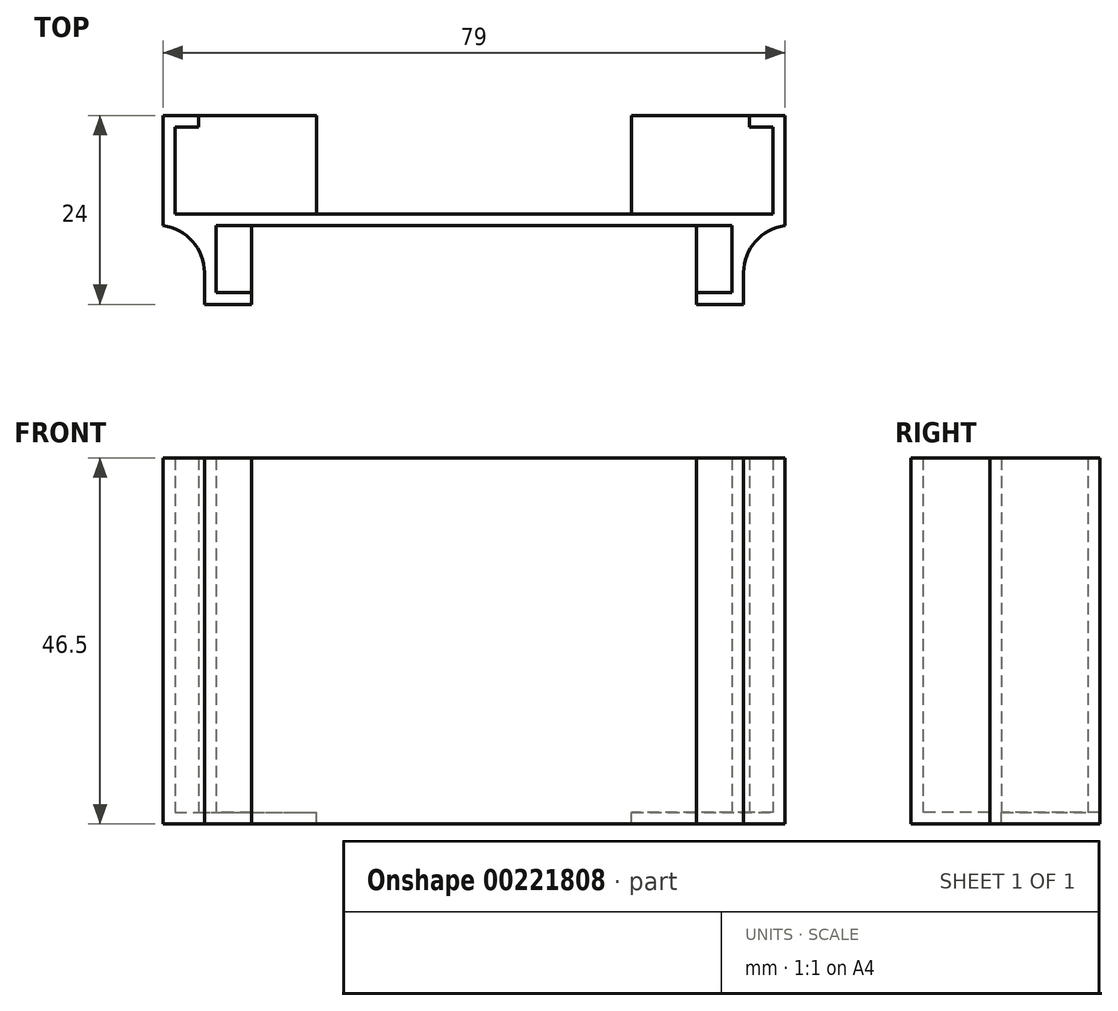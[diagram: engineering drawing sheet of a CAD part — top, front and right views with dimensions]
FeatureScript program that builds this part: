
annotation { "Feature Type Name" : "Feature", "Feature Type Description" : "" }
export const myFeature = defineFeature(function(context is Context, id is Id, definition is map)
    precondition{}
    {
        {
            var Q0;
            Q0=qCreatedBy(makeId("Top.planeOp"),FACE);
            var sketch = newSketch(context, id + "F0", { "sketchPlane" : qUnion([Q0])});
            skLineSegment(sketch, "E0", {"start": v(0, 0) * mm, "end": v(-38, 0) * mm});
            skLineSegment(sketch, "E1", {"start": v(-38, 0) * mm, "end": v(-38, 11) * mm});
            skLineSegment(sketch, "E2", {"start": v(-38, 11) * mm, "end": v(-35, 11) * mm});
            skLineSegment(sketch, "E3.0", {"start": v(-39.5, 12.5) * mm, "end": v(-35, 12.5) * mm});
            skLineSegment(sketch, "E3.1", {"start": v(-39.5, -1.5) * mm, "end": v(-39.5, 12.5) * mm});
            skLineSegment(sketch, "E3.2", {"start": v(0, -1.5) * mm, "end": v(-39.5, -1.5) * mm});
            skLineSegment(sketch, "E4", {"start": v(-35, 12.5) * mm, "end": v(-35, 11) * mm});
            skLineSegment(sketch, "E5.MirrorCS", {"start": v(0, 0) * mm, "end": v(38, 0) * mm});
            skLineSegment(sketch, "E6.MirrorCS", {"start": v(38, 0) * mm, "end": v(38, 11) * mm});
            skLineSegment(sketch, "E7.MirrorCS", {"start": v(38, 11) * mm, "end": v(35, 11) * mm});
            skLineSegment(sketch, "E8.MirrorCS", {"start": v(35, 12.5) * mm, "end": v(35, 11) * mm});
            skLineSegment(sketch, "E9.MirrorCS", {"start": v(39.5, 12.5) * mm, "end": v(35, 12.5) * mm});
            skLineSegment(sketch, "E10.MirrorCS", {"start": v(39.5, -1.5) * mm, "end": v(39.5, 12.5) * mm});
            skLineSegment(sketch, "E11.MirrorCS", {"start": v(0, -1.5) * mm, "end": v(39.5, -1.5) * mm});
            skLineSegment(sketch, "E12", {"start": v(-32.75, -1.5) * mm, "end": v(-32.75, -10) * mm});
            skLineSegment(sketch, "E13", {"start": v(-32.75, -10) * mm, "end": v(-28.25, -10) * mm});
            skLineSegment(sketch, "E14.0", {"start": v(-34.25, -11.5) * mm, "end": v(-28.25, -11.5) * mm});
            skLineSegment(sketch, "E14.1", {"start": v(-34.25, -1.5) * mm, "end": v(-34.25, -11.5) * mm});
            skLineSegment(sketch, "E15", {"start": v(-28.25, -10) * mm, "end": v(-28.25, -11.5) * mm});
            skLineSegment(sketch, "E16.MirrorCS", {"start": v(34.25, -1.5) * mm, "end": v(34.25, -11.5) * mm});
            skLineSegment(sketch, "E17.MirrorCS", {"start": v(32.75, -1.5) * mm, "end": v(32.75, -10) * mm});
            skLineSegment(sketch, "E18.MirrorCS", {"start": v(32.75, -10) * mm, "end": v(28.25, -10) * mm});
            skLineSegment(sketch, "E19.MirrorCS", {"start": v(34.25, -11.5) * mm, "end": v(28.25, -11.5) * mm});
            skLineSegment(sketch, "E20.MirrorCS", {"start": v(28.25, -10) * mm, "end": v(28.25, -11.5) * mm});
            skSolve(sketch);
        }
        {
            var Q0;
            Q0=makeQuery(id+"F0.imprint","IMPRINT",FACE,{"disambiguationData":[TD([[makeQuery(id+"F0.imprint","IMPRINT",EDGE,{"derivedFrom":sQuery(id+"F0.wireOp",EDGE,"E0")}),1.0]])]});
            var Q1;
            {var subQ0=sQuery(id+"F0.wireOp",EDGE,"E12");Q1=makeQuery(id+"F0.imprint","IMPRINT",FACE,{"disambiguationData":[TD([[makeQuery(id+"F0.imprint","IMPRINT",EDGE,{"derivedFrom":subQ0}),-1.0]])]});}
            var Q2;
            {var subQ1=sQuery(id+"F0.wireOp",EDGE,"E16.MirrorCS");Q2=makeQuery(id+"F0.imprint","IMPRINT",FACE,{"disambiguationData":[TD([[makeQuery(id+"F0.imprint","IMPRINT",EDGE,{"derivedFrom":subQ1}),-1.0]])]});}
            extrude(context, id + "F1", {"entities" : qUnion([Q0, Q1, Q2]), "depth" : 45 * mm});
        }
        {
            var Q0;
            Q0=makeQuery(id+"F1.opExtrude","SWEPT_EDGE",EDGE,{"disambiguationData":[OSD([sQuery(id+"F0.wireOp",EDGE,"E3.2"),sQuery(id+"F0.wireOp",EDGE,"E14.1")])]});
            var Q1;
            Q1=makeQuery(id+"F1.opExtrude","SWEPT_EDGE",EDGE,{"disambiguationData":[OSD([sQuery(id+"F0.wireOp",EDGE,"E11.MirrorCS"),sQuery(id+"F0.wireOp",EDGE,"E16.MirrorCS")])]});
            fillet(context, id + "F2", {"entities" : qUnion([Q0, Q1]), "radius" : 6 * mm, "tangentPropagation" : true, "allowEdgeOverflow" : false});
        }
        {
            var Q0;
            Q0=makeQuery(id+"F1.opExtrude","CAP_FACE",FACE,{"disambiguationData":[OSD([sQuery(id+"F0.wireOp",EDGE,"E0"),sQuery(id+"F0.wireOp",EDGE,"E1"),sQuery(id+"F0.wireOp",EDGE,"E2"),sQuery(id+"F0.wireOp",EDGE,"E3.0"),sQuery(id+"F0.wireOp",EDGE,"E3.1"),sQuery(id+"F0.wireOp",EDGE,"E3.2"),sQuery(id+"F0.wireOp",EDGE,"E4"),sQuery(id+"F0.wireOp",EDGE,"E5.MirrorCS"),sQuery(id+"F0.wireOp",EDGE,"E6.MirrorCS"),sQuery(id+"F0.wireOp",EDGE,"E7.MirrorCS"),sQuery(id+"F0.wireOp",EDGE,"E8.MirrorCS"),sQuery(id+"F0.wireOp",EDGE,"E9.MirrorCS"),sQuery(id+"F0.wireOp",EDGE,"E10.MirrorCS"),sQuery(id+"F0.wireOp",EDGE,"E11.MirrorCS"),sQuery(id+"F0.wireOp",EDGE,"E12"),sQuery(id+"F0.wireOp",EDGE,"E13"),sQuery(id+"F0.wireOp",EDGE,"E14.0"),sQuery(id+"F0.wireOp",EDGE,"E14.1"),sQuery(id+"F0.wireOp",EDGE,"E15"),sQuery(id+"F0.wireOp",EDGE,"E16.MirrorCS"),sQuery(id+"F0.wireOp",EDGE,"E17.MirrorCS"),sQuery(id+"F0.wireOp",EDGE,"E18.MirrorCS"),sQuery(id+"F0.wireOp",EDGE,"E19.MirrorCS"),sQuery(id+"F0.wireOp",EDGE,"E20.MirrorCS")])],"isStart":true});
            var sketch = newSketch(context, id + "F3", { "sketchPlane" : qUnion([Q0])});
            skLineSegment(sketch, "E21", {"start": v(-35, -12.5) * mm, "end": v(-20, -12.5) * mm});
            skLineSegment(sketch, "E22", {"start": v(-20, -12.5) * mm, "end": v(-20, 0) * mm});
            skLineSegment(sketch, "E23", {"start": v(-28.25, 10) * mm, "end": v(-28.25, 1.5) * mm});
            skLineSegment(sketch, "E24.MirrorCS", {"start": v(28.25, 10) * mm, "end": v(28.25, 1.5) * mm});
            skLineSegment(sketch, "E25.MirrorCS", {"start": v(20, -12.5) * mm, "end": v(20, 0) * mm});
            skLineSegment(sketch, "E26.MirrorCS", {"start": v(35, -12.5) * mm, "end": v(20, -12.5) * mm});
            skSolve(sketch);
        }
        {
            var Q0;
            {var subQ22=sQuery(id+"F0.wireOp",EDGE,"E1");var subQ27=makeQuery(id+"F1.opExtrude","CAP_EDGE",EDGE,{"disambiguationData":[OSD([subQ22])],"isStart":true});Q0=makeQuery(id+"F3.imprint","IMPRINT",FACE,{"disambiguationData":[TD([[makeQuery(id+"F3.imprint","IMPRINT",EDGE,{"derivedFrom":subQ27}),-1.0]])]});}
            var Q1;
            {var subQ0=sQuery(id+"F3.wireOp",EDGE,"E23");Q1=makeQuery(id+"F3.imprint","IMPRINT",FACE,{"disambiguationData":[TD([[makeQuery(id+"F3.imprint","IMPRINT",EDGE,{"derivedFrom":subQ0}),-1.0]])]});}
            var Q2;
            Q2=makeQuery(id+"F3.imprint","IMPRINT",FACE,{"disambiguationData":[TD([[makeQuery(id+"F3.imprint","IMPRINT",EDGE,{"derivedFrom":sQuery(id+"F3.wireOp",EDGE,"E21")}),1.0]])]});
            var Q3;
            {var subQ1=sQuery(id+"F3.wireOp",EDGE,"E25.MirrorCS");Q3=makeQuery(id+"F3.imprint","IMPRINT",FACE,{"disambiguationData":[TD([[makeQuery(id+"F3.imprint","IMPRINT",EDGE,{"derivedFrom":subQ1}),-1.0]])]});}
            var Q4;
            {var subQ0=sQuery(id+"F3.wireOp",EDGE,"E24.MirrorCS");Q4=makeQuery(id+"F3.imprint","IMPRINT",FACE,{"disambiguationData":[TD([[makeQuery(id+"F3.imprint","IMPRINT",EDGE,{"derivedFrom":subQ0}),1.0]])]});}
            extrude(context, id + "F4", {"entities" : qUnion([Q0, Q1, Q2, Q3, Q4]), "operationType" : NewBodyOperationType.ADD, "depth" : 1.5 * mm});
        }
    });
